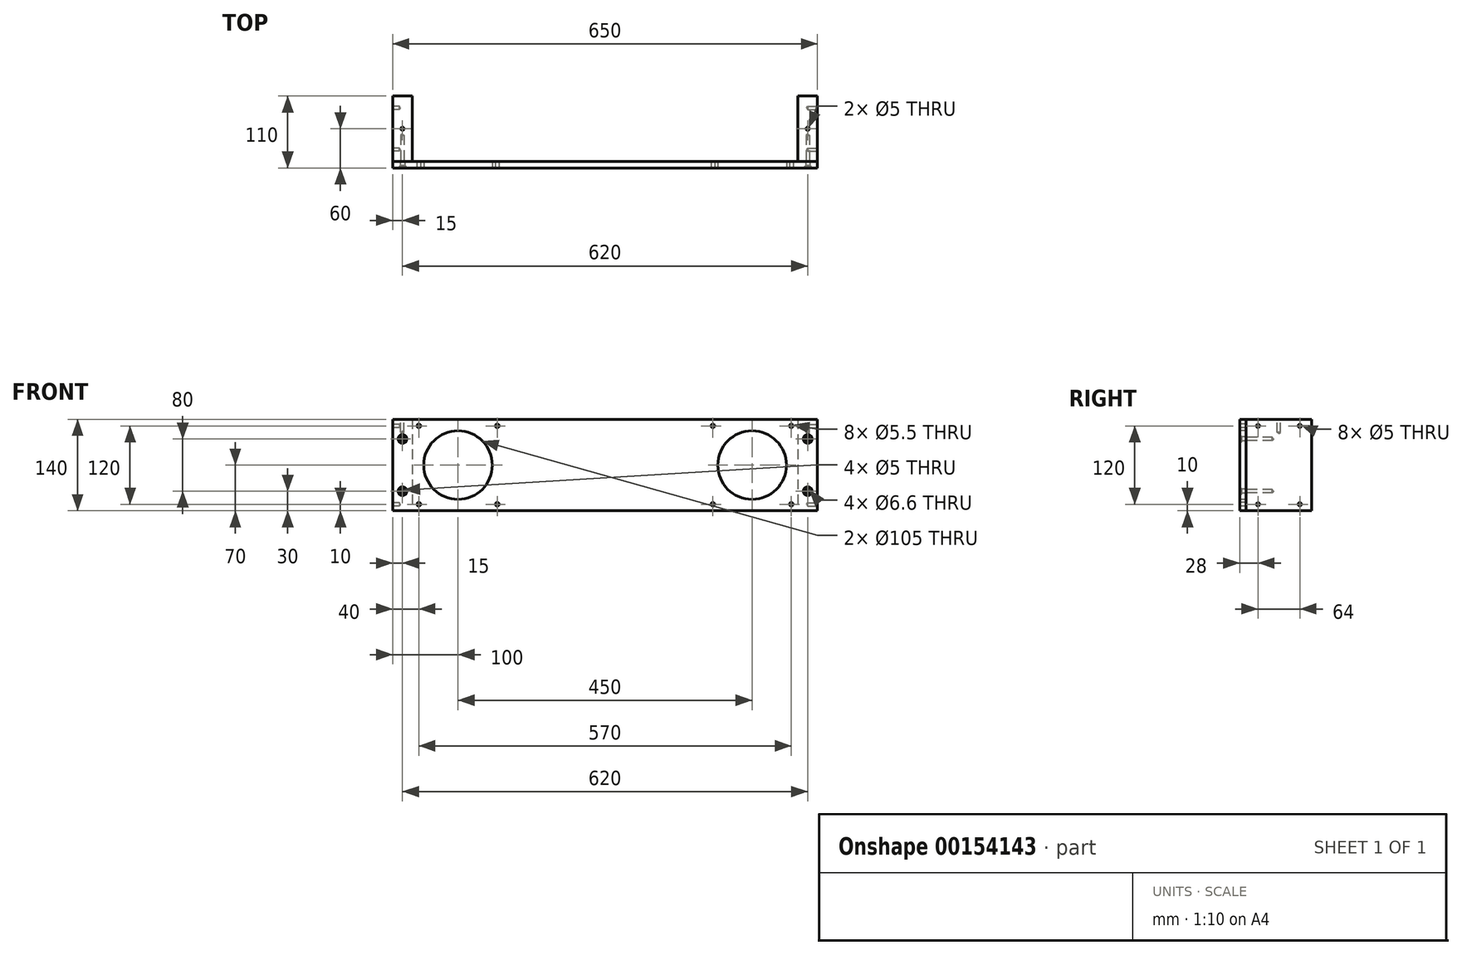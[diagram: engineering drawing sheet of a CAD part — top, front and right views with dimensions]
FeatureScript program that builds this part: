
annotation { "Feature Type Name" : "Feature", "Feature Type Description" : "" }
export const myFeature = defineFeature(function(context is Context, id is Id, definition is map)
    precondition{}
    {
        {
            var Q0;
            Q0=qCreatedBy(makeId("Front.planeOp"),FACE);
            var sketch = newSketch(context, id + "F0", { "sketchPlane" : qUnion([Q0])});
            skLineSegment(sketch, "E0.bottom", {"start": v(325, -70) * mm, "end": v(-325, -70) * mm});
            skLineSegment(sketch, "E0.top", {"start": v(325, 70) * mm, "end": v(-325, 70) * mm});
            skLineSegment(sketch, "E0.left", {"start": v(325, -70) * mm, "end": v(325, 70) * mm});
            skLineSegment(sketch, "E0.right", {"start": v(-325, -70) * mm, "end": v(-325, 70) * mm});
            skPoint(sketch, "E0.middle", {"position": v(0, 0) * mm});
            skPoint(sketch, "E1", {"position": v(-310, 40) * mm});
            skPoint(sketch, "E2", {"position": v(-310, -40) * mm});
            skPoint(sketch, "E3", {"position": v(310, 40) * mm});
            skPoint(sketch, "E4", {"position": v(310, -40) * mm});
            skPoint(sketch, "E5", {"position": v(-225, 0) * mm});
            skPoint(sketch, "E6", {"position": v(225, 0) * mm});
            skLineSegment(sketch, "E7.bottom", {"start": v(-165, -60) * mm, "end": v(-285, -60) * mm});
            skLineSegment(sketch, "E7.top", {"start": v(-165, 60) * mm, "end": v(-285, 60) * mm});
            skLineSegment(sketch, "E7.left", {"start": v(-165, -60) * mm, "end": v(-165, 60) * mm});
            skLineSegment(sketch, "E7.right", {"start": v(-285, -60) * mm, "end": v(-285, 60) * mm});
            skLineSegment(sketch, "E8.bottom", {"start": v(285, -60) * mm, "end": v(165, -60) * mm});
            skLineSegment(sketch, "E8.top", {"start": v(285, 60) * mm, "end": v(165, 60) * mm});
            skLineSegment(sketch, "E8.left", {"start": v(285, -60) * mm, "end": v(285, 60) * mm});
            skLineSegment(sketch, "E8.right", {"start": v(165, -60) * mm, "end": v(165, 60) * mm});
            skSolve(sketch);
        }
        {
            var Q0;
            Q0 = qSketchRegion(id + "F0", true);
            var Q1;
            Q1=makeQuery(id+"F0.imprint","IMPRINT",FACE,{"disambiguationData":[TD([[makeQuery(id+"F0.imprint","IMPRINT",EDGE,{"derivedFrom":sQuery(id+"F0.wireOp",EDGE,"E7.bottom")}),-1.0]])]});
            var Q2;
            Q2=makeQuery(id+"F0.imprint","IMPRINT",FACE,{"disambiguationData":[TD([[makeQuery(id+"F0.imprint","IMPRINT",EDGE,{"derivedFrom":sQuery(id+"F0.wireOp",EDGE,"E8.bottom")}),-1.0]])]});
            extrude(context, id + "F1", {"entities" : qUnion([Q0, Q1, Q2]), "oppositeDirection" : true, "depth" : 10 * mm});
        }
        {
            var Q0;
            Q0=makeQuery(id+"F1.opExtrude","SWEPT_BODY",BODY,{"disambiguationData":[OSD([sQuery(id+"F0.wireOp",EDGE,"E0.bottom"),sQuery(id+"F0.wireOp",EDGE,"E0.top"),sQuery(id+"F0.wireOp",EDGE,"E0.left"),sQuery(id+"F0.wireOp",EDGE,"E0.right")])]});
            transform(context, id + "F2", {"entities" : qUnion([Q0]), "transformType" : TransformType.TRANSLATION_3D, "dx" : 0 * mm, "dy" : 0 * mm, "dz" : 10 * mm, "makeCopy" : true});
        }
        {
            var Q0;
            Q0=makeQuery(id+"F2.opPattern","COPY",BODY,{"derivedFrom":makeQuery(id+"F1.opExtrude","SWEPT_BODY",BODY,{"disambiguationData":[OSD([sQuery(id+"F0.wireOp",EDGE,"E0.bottom"),sQuery(id+"F0.wireOp",EDGE,"E0.top"),sQuery(id+"F0.wireOp",EDGE,"E0.left"),sQuery(id+"F0.wireOp",EDGE,"E0.right")])]}),"instanceName":"1"});
            deleteBodies(context, id + "F3", {"entities" : qUnion([Q0])});
        }
        {
            var Q0;
            Q0=makeQuery(id+"F1.opExtrude","CAP_FACE",FACE,{"disambiguationData":[OSD([sQuery(id+"F0.wireOp",EDGE,"E0.bottom"),sQuery(id+"F0.wireOp",EDGE,"E0.top"),sQuery(id+"F0.wireOp",EDGE,"E0.left"),sQuery(id+"F0.wireOp",EDGE,"E0.right")])],"isStart":false});
            var sketch = newSketch(context, id + "F4", { "sketchPlane" : qUnion([Q0])});
            skLineSegment(sketch, "E9.left", {"start": v(325, 70) * mm, "end": v(325, -70) * mm});
            skLineSegment(sketch, "E10.bottom", {"start": v(325, 70) * mm, "end": v(295, 70) * mm});
            skLineSegment(sketch, "E10.top", {"start": v(325, -70) * mm, "end": v(295, -70) * mm});
            skLineSegment(sketch, "E10.right", {"start": v(295, 70) * mm, "end": v(295, -70) * mm});
            skLineSegment(sketch, "E11.bottom", {"start": v(-325, 70) * mm, "end": v(-295, 70) * mm});
            skLineSegment(sketch, "E11.top", {"start": v(-325, -70) * mm, "end": v(-295, -70) * mm});
            skLineSegment(sketch, "E11.left", {"start": v(-325, 70) * mm, "end": v(-325, -70) * mm});
            skLineSegment(sketch, "E11.right", {"start": v(-295, 70) * mm, "end": v(-295, -70) * mm});
            skSolve(sketch);
        }
        {
            var Q0;
            Q0 = qSketchRegion(id + "F4", true);
            extrude(context, id + "F5", {"entities" : qUnion([Q0]), "depth" : 100 * mm});
        }
        {
            var Q0;
            Q0=sQuery(id+"F0.wireOp",VERTEX,"E1");
            var Q1;
            Q1=sQuery(id+"F0.wireOp",VERTEX,"E2");
            var Q2;
            Q2=sQuery(id+"F0.wireOp",VERTEX,"E3");
            var Q3;
            Q3=sQuery(id+"F0.wireOp",VERTEX,"E4");
            var Q4;
            Q4=makeQuery(id+"F1.opExtrude","SWEPT_BODY",BODY,{"disambiguationData":[OSD([sQuery(id+"F0.wireOp",EDGE,"E0.bottom"),sQuery(id+"F0.wireOp",EDGE,"E0.top"),sQuery(id+"F0.wireOp",EDGE,"E0.left"),sQuery(id+"F0.wireOp",EDGE,"E0.right")])]});
            hole(context, id + "F6", {"style" : HoleStyle.C_SINK, "endStyle" : HoleEndStyle.BLIND, "standardTappedOrClearance" : lookupTablePath({ "standard" : "ISO", "fit" : "Normal", "size" : "M6", "type" : "Clearance" }), "standardBlindInLast" : lookupTablePath({ "fit" : "Standard", "standard" : "ISO", "size" : "M6", "type" : "Clearance" }), "holeDiameter" : 6.6 * mm, "cSinkDiameter" : 13.44 * mm, "cSinkAngle" : 90 * degree, "holeDepth" : 40 * mm, "locations" : qUnion([Q0, Q1, Q2, Q3]), "scope" : qUnion([Q4])});
        }
        {
            var Q0;
            Q0=makeQuery(id+"F5.opExtrude","SWEPT_FACE",FACE,{"disambiguationData":[OSD([sQuery(id+"F4.wireOp",EDGE,"E9.left")])]});
            var sketch = newSketch(context, id + "F7", { "sketchPlane" : qUnion([Q0])});
            skPoint(sketch, "E12", {"position": v(-92, 60) * mm});
            skPoint(sketch, "E13", {"position": v(-28, 60) * mm});
            skPoint(sketch, "E14", {"position": v(-92, -60) * mm});
            skPoint(sketch, "E15", {"position": v(-28, -60) * mm});
            skLineSegment(sketch, "E16", {"start": v(-92, 60) * mm, "end": v(-28, 60) * mm});
            skLineSegment(sketch, "E17", {"start": v(-28, 60) * mm, "end": v(-28, -60) * mm});
            skLineSegment(sketch, "E18", {"start": v(-92, -60) * mm, "end": v(-92, 60) * mm});
            skLineSegment(sketch, "E19", {"start": v(-92, -60) * mm, "end": v(-28, -60) * mm});
            skSolve(sketch);
        }
        {
            var Q0;
            Q0=sQuery(id+"F7.wireOp",VERTEX,"E12");
            var Q1;
            Q1=sQuery(id+"F7.wireOp",VERTEX,"E13");
            var Q2;
            Q2=sQuery(id+"F7.wireOp",VERTEX,"E15");
            var Q3;
            Q3=sQuery(id+"F7.wireOp",VERTEX,"E14");
            var Q4;
            Q4=makeQuery(id+"F5.opExtrude","SWEPT_BODY",BODY,{"disambiguationData":[OSD([sQuery(id+"F4.wireOp",EDGE,"E10.bottom"),sQuery(id+"F4.wireOp",EDGE,"E10.top"),sQuery(id+"F4.wireOp",EDGE,"E9.left"),sQuery(id+"F4.wireOp",EDGE,"E10.right")])]});
            hole(context, id + "F8", {"style" : HoleStyle.SIMPLE, "endStyle" : HoleEndStyle.BLIND, "standardTappedOrClearance" : lookupTablePath({ "standard" : "ISO", "engagement" : "75%", "pitch" : "1 mm", "size" : "M6", "type" : "Tapped" }), "standardBlindInLast" : lookupTablePath({ "standard" : "ISO", "engagement" : "75%", "pitch" : "1 mm", "size" : "M6", "type" : "Tapped" }), "holeDiameter" : 5 * mm, "holeDepth" : 10 * mm, "locations" : qUnion([Q0, Q1, Q2, Q3]), "scope" : qUnion([Q4]), "majorDiameter" : 6 * mm});
        }
        {
            var Q0;
            Q0=makeQuery(id+"F5.opExtrude","SWEPT_FACE",FACE,{"disambiguationData":[OSD([sQuery(id+"F4.wireOp",EDGE,"E11.left")])]});
            var sketch = newSketch(context, id + "F9", { "sketchPlane" : qUnion([Q0])});
            skPoint(sketch, "E20", {"position": v(28, 60) * mm});
            skPoint(sketch, "E21", {"position": v(92, 60) * mm});
            skPoint(sketch, "E22", {"position": v(28, -60) * mm});
            skPoint(sketch, "E23", {"position": v(92, -60) * mm});
            skLineSegment(sketch, "E24", {"start": v(28, 60) * mm, "end": v(92, 60) * mm});
            skLineSegment(sketch, "E25", {"start": v(92, 60) * mm, "end": v(92, -60) * mm});
            skLineSegment(sketch, "E26", {"start": v(28, -60) * mm, "end": v(28, 60) * mm});
            skLineSegment(sketch, "E27", {"start": v(28, -60) * mm, "end": v(92, -60) * mm});
            skSolve(sketch);
        }
        {
            var Q0;
            Q0=sQuery(id+"F9.wireOp",VERTEX,"E20");
            var Q1;
            Q1=sQuery(id+"F9.wireOp",VERTEX,"E21");
            var Q2;
            Q2=sQuery(id+"F9.wireOp",VERTEX,"E23");
            var Q3;
            Q3=sQuery(id+"F9.wireOp",VERTEX,"E22");
            var Q4;
            Q4=makeQuery(id+"F5.opExtrude","SWEPT_BODY",BODY,{"disambiguationData":[OSD([sQuery(id+"F4.wireOp",EDGE,"E11.bottom"),sQuery(id+"F4.wireOp",EDGE,"E11.top"),sQuery(id+"F4.wireOp",EDGE,"E11.left"),sQuery(id+"F4.wireOp",EDGE,"E11.right")])]});
            hole(context, id + "F10", {"style" : HoleStyle.SIMPLE, "endStyle" : HoleEndStyle.BLIND, "standardTappedOrClearance" : lookupTablePath({ "standard" : "ISO", "engagement" : "75%", "pitch" : "1 mm", "size" : "M6", "type" : "Tapped" }), "standardBlindInLast" : lookupTablePath({ "standard" : "ISO", "engagement" : "75%", "pitch" : "1 mm", "size" : "M6", "type" : "Tapped" }), "holeDiameter" : 5 * mm, "holeDepth" : 15 * mm, "locations" : qUnion([Q0, Q1, Q2, Q3]), "scope" : qUnion([Q4]), "majorDiameter" : 6 * mm});
        }
        {
            var Q0;
            Q0=sQuery(id+"F0.wireOp",VERTEX,"E5");
            var Q1;
            Q1=sQuery(id+"F0.wireOp",VERTEX,"E6");
            var Q2;
            Q2=makeQuery(id+"F1.opExtrude","SWEPT_BODY",BODY,{"disambiguationData":[OSD([sQuery(id+"F0.wireOp",EDGE,"E0.bottom"),sQuery(id+"F0.wireOp",EDGE,"E0.top"),sQuery(id+"F0.wireOp",EDGE,"E0.left"),sQuery(id+"F0.wireOp",EDGE,"E0.right")])]});
            hole(context, id + "F11", {"style" : HoleStyle.SIMPLE, "endStyle" : HoleEndStyle.THROUGH, "holeDiameter" : 105 * mm, "locations" : qUnion([Q0, Q1]), "scope" : qUnion([Q2]), "isTappedThrough" : true});
        }
        {
            var Q0;
            Q0=sQuery(id+"F0.wireOp",VERTEX,"E1");
            var Q1;
            Q1=sQuery(id+"F0.wireOp",VERTEX,"E2");
            var Q2;
            Q2=sQuery(id+"F0.wireOp",VERTEX,"E3");
            var Q3;
            Q3=sQuery(id+"F0.wireOp",VERTEX,"E4");
            var Q4;
            Q4=makeQuery(id+"F5.opExtrude","SWEPT_BODY",BODY,{"disambiguationData":[OSD([sQuery(id+"F4.wireOp",EDGE,"E11.bottom"),sQuery(id+"F4.wireOp",EDGE,"E11.top"),sQuery(id+"F4.wireOp",EDGE,"E11.left"),sQuery(id+"F4.wireOp",EDGE,"E11.right")])]});
            var Q5;
            Q5=makeQuery(id+"F5.opExtrude","SWEPT_BODY",BODY,{"disambiguationData":[OSD([sQuery(id+"F4.wireOp",EDGE,"E10.bottom"),sQuery(id+"F4.wireOp",EDGE,"E10.top"),sQuery(id+"F4.wireOp",EDGE,"E9.left"),sQuery(id+"F4.wireOp",EDGE,"E10.right")])]});
            hole(context, id + "F12", {"style" : HoleStyle.SIMPLE, "endStyle" : HoleEndStyle.BLIND, "standardTappedOrClearance" : lookupTablePath({ "standard" : "ISO", "engagement" : "75%", "pitch" : "1 mm", "size" : "M6", "type" : "Tapped" }), "standardBlindInLast" : lookupTablePath({ "standard" : "ISO", "engagement" : "75%", "pitch" : "1 mm", "size" : "M6", "type" : "Tapped" }), "holeDiameter" : 5 * mm, "holeDepth" : 40 * mm, "locations" : qUnion([Q0, Q1, Q2, Q3]), "scope" : qUnion([Q4, Q5]), "majorDiameter" : 6 * mm});
        }
        {
            var Q0;
            Q0=makeQuery(id+"F5.opExtrude","SWEPT_FACE",FACE,{"disambiguationData":[OSD([sQuery(id+"F4.wireOp",EDGE,"E10.bottom")])]});
            var sketch = newSketch(context, id + "F13", { "sketchPlane" : qUnion([Q0])});
            skPoint(sketch, "E28", {"position": v(-310, 60) * mm});
            skPoint(sketch, "E29", {"position": v(310, 60) * mm});
            skSolve(sketch);
        }
        {
            var Q0;
            Q0=sQuery(id+"F13.wireOp",VERTEX,"E28");
            var Q1;
            Q1=sQuery(id+"F13.wireOp",VERTEX,"E29");
            var Q2;
            Q2=makeQuery(id+"F5.opExtrude","SWEPT_BODY",BODY,{"disambiguationData":[OSD([sQuery(id+"F4.wireOp",EDGE,"E10.bottom"),sQuery(id+"F4.wireOp",EDGE,"E10.top"),sQuery(id+"F4.wireOp",EDGE,"E9.left"),sQuery(id+"F4.wireOp",EDGE,"E10.right")])]});
            var Q3;
            Q3=makeQuery(id+"F5.opExtrude","SWEPT_BODY",BODY,{"disambiguationData":[OSD([sQuery(id+"F4.wireOp",EDGE,"E11.bottom"),sQuery(id+"F4.wireOp",EDGE,"E11.top"),sQuery(id+"F4.wireOp",EDGE,"E11.left"),sQuery(id+"F4.wireOp",EDGE,"E11.right")])]});
            hole(context, id + "F14", {"style" : HoleStyle.SIMPLE, "endStyle" : HoleEndStyle.BLIND, "standardTappedOrClearance" : lookupTablePath({ "standard" : "ISO", "engagement" : "75%", "pitch" : "1 mm", "size" : "M6", "type" : "Tapped" }), "standardBlindInLast" : lookupTablePath({ "standard" : "ISO", "engagement" : "75%", "pitch" : "1 mm", "size" : "M6", "type" : "Tapped" }), "holeDiameter" : 5 * mm, "holeDepth" : 20 * mm, "locations" : qUnion([Q0, Q1]), "scope" : qUnion([Q2, Q3]), "majorDiameter" : 6 * mm});
        }
        {
            var Q0;
            Q0=sQuery(id+"F0.wireOp",VERTEX,"E7.left.end");
            var Q1;
            Q1=sQuery(id+"F0.wireOp",VERTEX,"E7.right.end");
            var Q2;
            Q2=sQuery(id+"F0.wireOp",VERTEX,"E7.right.start");
            var Q3;
            Q3=sQuery(id+"F0.wireOp",VERTEX,"E7.left.start");
            var Q4;
            Q4=sQuery(id+"F0.wireOp",VERTEX,"E8.right.end");
            var Q5;
            Q5=sQuery(id+"F0.wireOp",VERTEX,"E8.top.start");
            var Q6;
            Q6=sQuery(id+"F0.wireOp",VERTEX,"E8.bottom.start");
            var Q7;
            Q7=sQuery(id+"F0.wireOp",VERTEX,"E8.bottom.end");
            var Q8;
            Q8=makeQuery(id+"F1.opExtrude","SWEPT_BODY",BODY,{"disambiguationData":[OSD([sQuery(id+"F0.wireOp",EDGE,"E0.bottom"),sQuery(id+"F0.wireOp",EDGE,"E0.top"),sQuery(id+"F0.wireOp",EDGE,"E0.left"),sQuery(id+"F0.wireOp",EDGE,"E0.right")])]});
            hole(context, id + "F15", {"style" : HoleStyle.SIMPLE, "endStyle" : HoleEndStyle.THROUGH, "standardTappedOrClearance" : lookupTablePath({ "standard" : "ISO", "fit" : "Normal", "size" : "M5", "type" : "Clearance" }), "standardBlindInLast" : lookupTablePath({ "fit" : "Standard", "standard" : "ISO", "size" : "M5", "type" : "Clearance" }), "holeDiameter" : 5.5 * mm, "locations" : qUnion([Q0, Q1, Q2, Q3, Q4, Q5, Q6, Q7]), "scope" : qUnion([Q8]), "isTappedThrough" : true});
        }
    });
